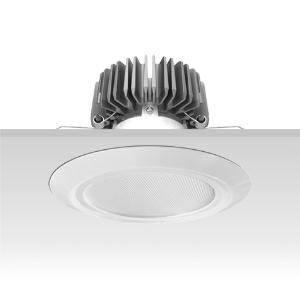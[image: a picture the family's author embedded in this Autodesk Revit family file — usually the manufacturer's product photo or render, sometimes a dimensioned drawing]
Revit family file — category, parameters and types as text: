
# Revit family: 3f_filippi_-_3f_reno_bianco_ampio_3f_filippi_-_30679_a01037_-_3f_reno_200_wh_3000-840_dali_wide___vs_wh_7c87
name_source: partatom
category: Lighting Fixtures
units: mm (PartAtom-declared; Revit-internal decimal feet)

## family parameters
Cut with Voids When Loaded = No
Host = Face
Light Source = No
Part Type = Normal
Room Calculation Point = No
Round Connector Dimension = Use Diameter
Shared = No

## types (1)
- 3F Filippi - 3F Reno Bianco Ampio (1 x LED, 2312 lm, 28 W, 4000 K)
    Apparent Load = 28 VA
    Approval mark = CE
    CIE Flux Codes = 75 94 99 100 100
    Color Rendering = 80
    Color Temperature = 4000 K
    Control Gear = Electronic transformer
    Default Elevation = 1800 mm
    Description = ILLUMINOTECHNICAL
Luminous efficiency 100% (DLOR 100%, ULOR 0%).
Initial luminous flux of the luminaire 2312 lm.
Direct symmetric wide distribution.
Installation Interdistance Transv.D = 1.16 x hu - Long.D = 1.14 x hu.
Tabular UGR (CIE 117 - 4H-8H; S=0.25H; 70/50/20): RUG 21.5 - 21.4.
Beam angle: 74° - 74°.
Luminous efficacy 83 lm/W.
Lifetime (L90/B10): 30000 h. (tq+25°C)
Lifetime (L85/B10): 50000 h. (tq+25°C)
Lifetime (L70/B10): 80000 h. (tq+25°C)
Sudden decreased luminous flux after 50000 hours: 0% (C0).
Photobiological safety in compliance with IEC/TR 62778: RG0 risk exempt, (IEC 62471).
In compliance with IEC/EN 62722-2-1 - IEC/EN 62717 standards.

SOURCE
Compact LED module 3000/840.
Energy efficiency class (UE 2019/2020 - UE 2019/2015): E.
CIE 13.3 Colour rendering index: CRI >80 (R9 <50%).
IES TM-30 Fidelity Index: Rf = 84 Rg = 95.
CCT nominal colour temperature 4000 K.
Colour initial tolerance (MacAdam): SDCM 3.
Zhaga Book 3 compliant.

MECHANICAL
Passive heat dissipator in die-casting aluminium, oversized, for optimum thermal management of the LED module.
Parabolic element with graduated/concentric rings in white polycarbonate.
Transparent external lens with glossy and satin differentiated surfaces, with a cooling and anti-insect system in methacrylate (PMMA).
Fastening spring clips in stainless steel.
Dimensions: diameter 226 mm, height 146 mm. Weight 1.85 kg.
IP44 protection degree for exposed part, IP20 for recessed part.
Mechanical strength to impacts IK06 (1 joule).
Glow-wire test resistance 650°C.

ELECTRICAL
Wiring on a separate unit.
Halogen Free DALI-2 DATI (Parts 251, 252, 253), PUSH-DIM, electronic wiring 230V-50/60Hz, power factor 0.97 at full load, THD <25%, constant output current, SELV, class II, 1 driver, 1 DALI addresse.
Power of the luminaire 28 W.
ENEC - CE.
SAFE FLICKER: PstLM=<1 and SVM=<0.4 (IEC TR 61547-1 and IEC TR 63158), to ensure a more comfortable and safe light.
Luminaire compliant with EN 60598-2-22 for power supply from a centralised emergency system CPSS (Central Power Supply System), not incorporated in the luminaire - high risk areas excluded. The default power and flux are 100% in AC and 100% in DC.
Ambient temperature from 0°C to +25°C.
Temperature class T6 max 85°C.
Relative humidity UR: <85%.

INSTALLATION
Pull-up recessed fitting.
False ceiling carving: 200 mm.
All accessories dedicated to this product are available on the Catalog and on our website www.3F-Filippi.com.

ACCESSORIES
A01037 - Anti-glare microprismatic VS moulded glass, tempered, not flammable, locked and in line with the trim, in white polycarbonate.

APPLICATIONS
Environments: architectural, commercial, exhibition areas, transit areas, corridors, shops, display windows, service areas.
In false ceilings with narrow voids.

LIGHT MANAGEMENT
Recommended minimum setting: 10%.
The luminaire, equipped with (DALI-2 DATI) driver, can be controlled manually with 3F Easy Dim technology or automatically/manually with wired or wireless DALI/D2D control systems.
The D2D driver guarantees interoperability with other devices with the same certification by making the following information available:
Device Data (Part 251), Energy Report (Part 252), Diagnosis & Maintenance (Part 253).
In electrical systems without a regulation system (manual or automatic) and DALI bus, a suitable jumper must be made on the DA-DA terminals of the appliance.

WARNING
Luminaire designed for disposal/recycling at end-of-life.
Replaceable (LED only) light source by a professional. Replaceable control gear by a professional.
    Height = 0 mm  [stored 0 ft]
    Lamp = 1 x LED
    Lamp Light Flux = 2312 lm
    Lamp Power = 28 W
    Lamp count = 1
    Length = 226 mm
    Lifetime = 50000 h
    Luminous efficacy = 83 lm/W
    Manufacturer = 3F Filippi
    ModVariant = No
    Model = 3F Filippi - 30679+A01037 - 3F Reno 200 WH 3000-840 DALI WIDE + VS WH
    Mounting Place = Ceiling
    Mounting Type = Recessed
    Number of Poles = 1
    OnlyDefault = Yes
    Power Factor = 1
    Product Name = 3F Filippi - 3F Reno Bianco Ampio
    Product group = recessed luminaire
    ProductGroupID = 4
    Protection Class = Protection class II
    Protection Degree = IP 20
    RLX_Detail_Level = 1
    RLX_Emergency_Light_Flux = 0 lm
    RLX_Emergency_Type = 0
    RLX_Emergency_Type_DB = No
    RlxData = <blob elided: 96817 chars, md5=3a9f1618>
    Socket = socket
    Standby Power = 0 W
    System Light Flux = 2312 lm
    System Power = 28 W
    Type Comments = Product without accessories
    Type Image = 3ffilippi_3f_reno_200_wh_vs_smp.jpg
    URL = http://relux.com
    VarID = ---
    Voltage = 0 V
    Weight = 0.00 kg
    Width = 0 mm  [stored 0 ft]

note: [stored X ft] marks values corroborated as IEEE doubles in the binary element streams (Revit-internal decimal feet)

## geometry (parser evidence)
native form markers: Blend x4, Sweep x9
no freeform markers — native parametric forms only
